# Revit family: 71253USA_NEW
name_source: partatom
category: Plumbing Fixtures
revit_build: Autodesk Revit 2018 (Build: 20170223_1515(x64)
units: mm (PartAtom-declared; Revit-internal decimal feet)

## family parameters
Always vertical = No
Cut with Voids When Loaded = No
OmniClass Number = 23.45.00.00
OmniClass Title = Sanitary, Laundry, and Cleaning Equipment
Part Type = Normal
Room Calculation Point = No
Round Connector Dimension = Use Diameter
Shared = No
Work Plane-Based = Yes

## types (2) — shared parameters
Always visible = Yes
BIMobject category = Basins
Default Elevation = 1219.2 mm  [stored 4 ft]
Design country = Germany
EAN code = 4059625356166
Edition number = 1
GTIN code = https://4059625356180
IFC Classification = Sanitary Terminal
Installation instructions = https://www.hansgrohe.com
Manufacturer country = Germany
Manufacturer name = hansgrohe
Material secondary = Chrome
Product Guid = bdea9699-c2cb-4c43-928d-8a8e54f9a909
Product SKU = 71253USA
Product data url = https://www.bimobject.com
Product family = Logis
Product group = Basin mixers
Product name = 71253USA Logis Single lever basin mixer 110 Fine without waste set
Product url = https://www.hansgrohe.com
QR code = https://www.bimobject.com
Technical description = https://www.hansgrohe.com
Weight Net (Kg) = 1,1

## per-type parameters (varying)
| type | Material 1 |
| 001 Chrome | Hansgrohe - Logis - 001 Chrome |
| 821 Brushed Nickel | Hansgrohe - Logis - 821 Brushed Nickel |

note: [stored X ft] marks values corroborated as IEEE doubles in the binary element streams (Revit-internal decimal feet)

## geometry (parser evidence)
native form markers: Sweep x2
no freeform markers — native parametric forms only
